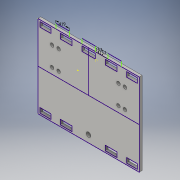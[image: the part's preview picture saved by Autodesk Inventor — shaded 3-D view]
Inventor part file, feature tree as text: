
AUTODESK INVENTOR PART (.ipt)
format: ipt  version: 2016 (Build 200138000, 138)  size: 200,704 bytes
history: native  units: in
note: dims shown in document units (in); Inventor stores cm internally (conversion verified against a paired STEP export)
features: sketch x5, extrude x2
ambient origin geometry x8: Origin, YZ Plane, XZ Plane, XY Plane, X Axis, Y Axis, Z Axis, Center Point
bodies: Solid1 (feature_tree)
feature tree (7):
  extrude  "Extrusion1"  Depth=2.6in
  extrude  "Extrusion2"  Depth=0.09in TaperAngle=0.0deg
  sketch  "Sketch3"  dims[d15=0.153in]
  sketch  "Sketch4"  dims[d16=0.09in d17=0.0in]
  sketch  "Sketch5"  dims[d23=0.419in d24=0.153in d25=0.153in]
  sketch  "Sketch1"  dims[d0=3.2in d1=2.6in]
  sketch  "Sketch2"  dims[d2=0.15in d9=0.09in d10=0.0in]
